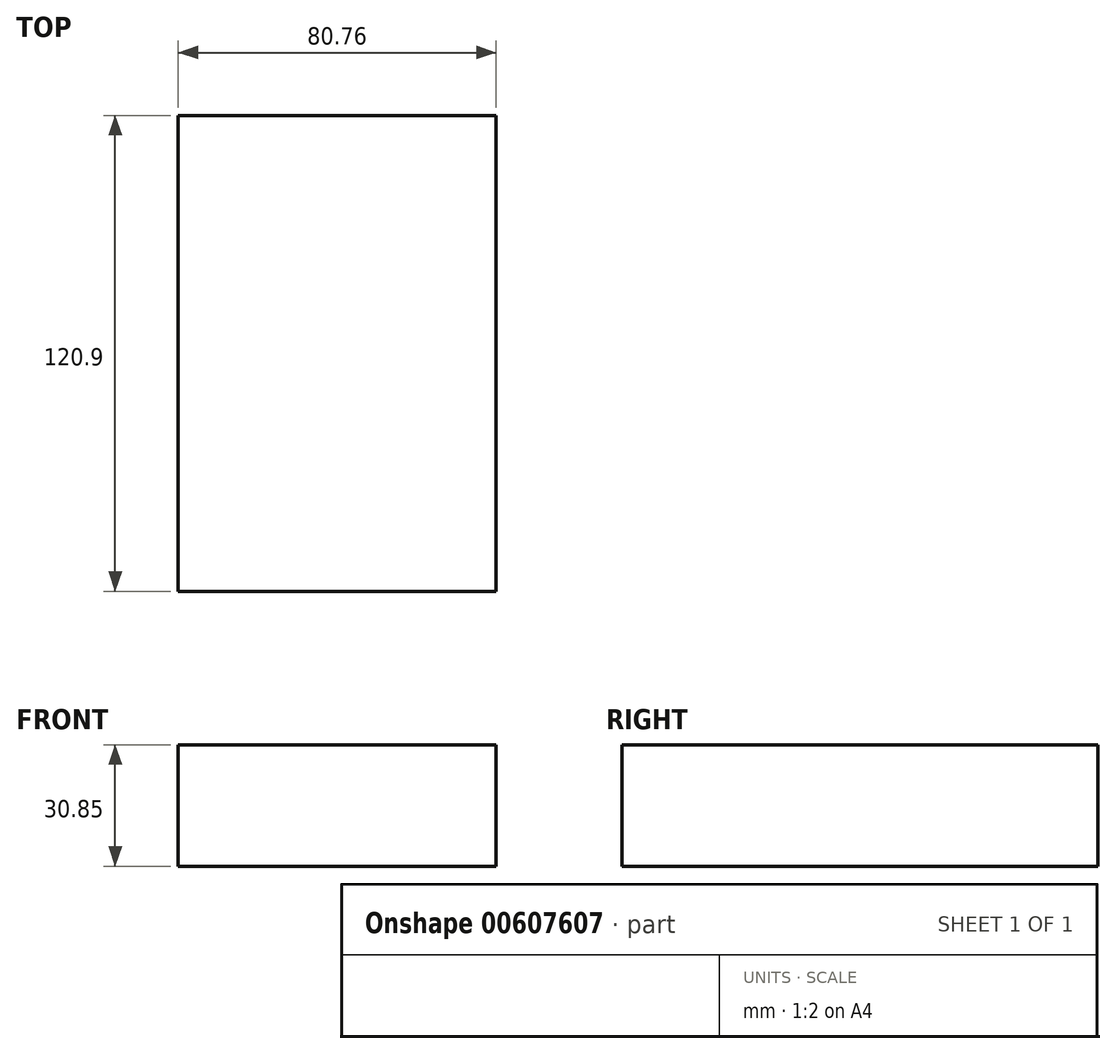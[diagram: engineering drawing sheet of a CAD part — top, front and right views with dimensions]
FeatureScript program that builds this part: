
annotation { "Feature Type Name" : "Feature", "Feature Type Description" : "" }
export const myFeature = defineFeature(function(context is Context, id is Id, definition is map)
    precondition{}
    {
        {
            var Q0;
            Q0=qCreatedBy(makeId("Front.planeOp"),FACE);
            var sketch = newSketch(context, id + "F0", { "sketchPlane" : qUnion([Q0])});
            skLineSegment(sketch, "E0.bottom", {"start": v(-54.05, 45.27) * mm, "end": v(26.71, 45.27) * mm});
            skLineSegment(sketch, "E0.top", {"start": v(-54.05, 14.42) * mm, "end": v(26.71, 14.42) * mm});
            skLineSegment(sketch, "E0.left", {"start": v(-54.05, 45.27) * mm, "end": v(-54.05, 14.42) * mm});
            skLineSegment(sketch, "E0.right", {"start": v(26.71, 45.27) * mm, "end": v(26.71, 14.42) * mm});
            skLineSegment(sketch, "E1.bottom", {"start": v(-17.43, 54.55) * mm, "end": v(26.71, 54.55) * mm});
            skLineSegment(sketch, "E1.left", {"start": v(-17.43, 54.55) * mm, "end": v(-17.43, 46.02) * mm});
            skLineSegment(sketch, "E1.right", {"start": v(26.71, 54.55) * mm, "end": v(26.71, 45.27) * mm});
            skSolve(sketch);
        }
        {
            var Q0;
            Q0=makeQuery(id+"F0.imprint","IMPRINT",FACE,{"disambiguationData":[TD([[makeQuery(id+"F0.imprint","IMPRINT",EDGE,{"derivedFrom":sQuery(id+"F0.wireOp",EDGE,"E0.bottom")}),-1.0]])]});
            var Q1;
            Q1=sQuery(id+"F0.wireOp",EDGE,"E0.bottom");
            var Q2;
            Q2=sQuery(id+"F0.wireOp",EDGE,"E0.left");
            var Q3;
            Q3=sQuery(id+"F0.wireOp",EDGE,"E0.top");
            var Q4;
            Q4=sQuery(id+"F0.wireOp",EDGE,"E0.right");
            extrude(context, id + "F1", {"entities" : qUnion([Q0]), "surfaceEntities" : qUnion([Q1, Q2, Q3, Q4]), "depth" : 120.9 * mm, "offsetDistance" : 25.4 * mm});
        }
    });
